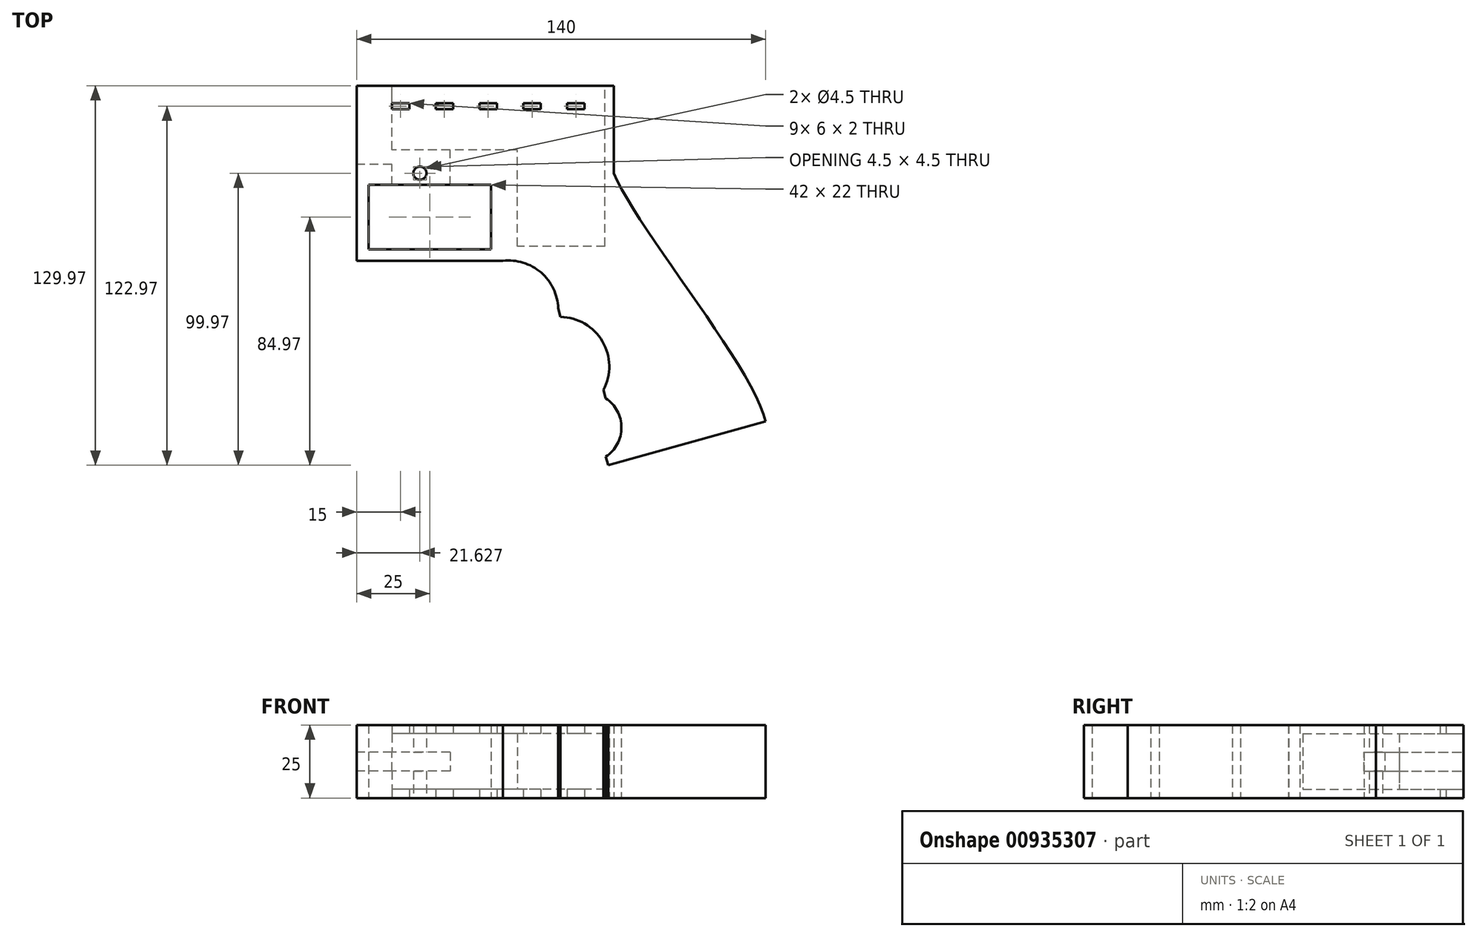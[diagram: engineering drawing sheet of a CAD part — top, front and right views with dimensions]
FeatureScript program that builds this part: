
annotation { "Feature Type Name" : "Feature", "Feature Type Description" : "" }
export const myFeature = defineFeature(function(context is Context, id is Id, definition is map)
    precondition{}
    {
        {
            var Q0;
            Q0=qCreatedBy(makeId("Top.planeOp"),FACE);
            var sketch = newSketch(context, id + "F0", { "sketchPlane" : qUnion([Q0])});
            skPoint(sketch, "E0", {"position": v(0, 0) * mm});
            skLineSegment(sketch, "E1.bottom", {"start": v(-44, 30) * mm, "end": v(44, 30) * mm});
            skLineSegment(sketch, "E1.top", {"start": v(-44, -30) * mm, "end": v(44, -30) * mm});
            skLineSegment(sketch, "E1.left", {"start": v(-44, 30) * mm, "end": v(-44, -30) * mm});
            skLineSegment(sketch, "E1.right", {"start": v(44, 30) * mm, "end": v(44, -30) * mm});
            skLineSegment(sketch, "E2.bottom", {"start": v(-40, -26) * mm, "end": v(2, -26) * mm});
            skLineSegment(sketch, "E2.top", {"start": v(-40, -4) * mm, "end": v(2, -4) * mm});
            skLineSegment(sketch, "E2.left", {"start": v(-40, -26) * mm, "end": v(-40, -4) * mm});
            skLineSegment(sketch, "E2.right", {"start": v(2, -26) * mm, "end": v(2, -4) * mm});
            skLineSegment(sketch, "E3.bottom", {"start": v(-32, 24) * mm, "end": v(-26, 24) * mm});
            skLineSegment(sketch, "E3.top", {"start": v(-32, 22) * mm, "end": v(-26, 22) * mm});
            skLineSegment(sketch, "E3.left", {"start": v(-32, 24) * mm, "end": v(-32, 22) * mm});
            skLineSegment(sketch, "E3.right", {"start": v(-26, 24) * mm, "end": v(-26, 22) * mm});
            skLineSegment(sketch, "E4.1.0.0", {"start": v(-17, 24) * mm, "end": v(-11, 24) * mm});
            skLineSegment(sketch, "E4.1.0.1", {"start": v(-17, 22) * mm, "end": v(-11, 22) * mm});
            skLineSegment(sketch, "E4.1.0.2", {"start": v(-11, 24) * mm, "end": v(-11, 22) * mm});
            skLineSegment(sketch, "E4.1.0.3", {"start": v(-17, 24) * mm, "end": v(-17, 22) * mm});
            skLineSegment(sketch, "E4.2.0.0", {"start": v(-2, 24) * mm, "end": v(4, 24) * mm});
            skLineSegment(sketch, "E4.2.0.1", {"start": v(-2, 22) * mm, "end": v(4, 22) * mm});
            skLineSegment(sketch, "E4.2.0.2", {"start": v(4, 24) * mm, "end": v(4, 22) * mm});
            skLineSegment(sketch, "E4.2.0.3", {"start": v(-2, 24) * mm, "end": v(-2, 22) * mm});
            skLineSegment(sketch, "E4.3.0.0", {"start": v(13, 24) * mm, "end": v(19, 24) * mm});
            skLineSegment(sketch, "E4.3.0.1", {"start": v(13, 22) * mm, "end": v(19, 22) * mm});
            skLineSegment(sketch, "E4.3.0.2", {"start": v(19, 24) * mm, "end": v(19, 22) * mm});
            skLineSegment(sketch, "E4.3.0.3", {"start": v(13, 24) * mm, "end": v(13, 22) * mm});
            skLineSegment(sketch, "E4.4.0.0", {"start": v(28, 24) * mm, "end": v(34, 24) * mm});
            skLineSegment(sketch, "E4.4.0.1", {"start": v(28, 22) * mm, "end": v(34, 22) * mm});
            skLineSegment(sketch, "E4.4.0.2", {"start": v(34, 24) * mm, "end": v(34, 22) * mm});
            skLineSegment(sketch, "E4.4.0.3", {"start": v(28, 24) * mm, "end": v(28, 22) * mm});
            skLineSegment(sketch, "E4.direction1", {"start": v(-32, 24) * mm, "end": v(-17, 24) * mm, "construction": true});
            skFitSpline(sketch, "E5", {"points": [v(44, 0) * mm, v(96, -85) * mm], "startDerivative": vector(23.47, -56.54) * mm, "endDerivative": vector(13.41, -56.5) * mm});
            skLineSegment(sketch, "E6", {"start": v(96, -85) * mm, "end": v(42.04, -99.97) * mm});
            skLineSegment(sketch, "E7", {"start": v(42.04, -99.97) * mm, "end": v(41.24, -97.08) * mm});
            skArc(sketch, "E8", {"start": v(41.24, -97.08) * mm, "mid": v(46.6, -87.08) * mm, "end": v(41.24, -77.08) * mm});
            skLineSegment(sketch, "E9", {"start": v(41.24, -77.08) * mm, "end": v(40.43, -74.2) * mm});
            skArc(sketch, "E10", {"start": v(40.43, -74.2) * mm, "mid": v(40.1, -57.58) * mm, "end": v(25.76, -49.2) * mm});
            skLineSegment(sketch, "E11", {"start": v(25.76, -49.2) * mm, "end": v(24.96, -46.3) * mm});
            skArc(sketch, "E12", {"start": v(24.96, -46.3) * mm, "mid": v(19.05, -34) * mm, "end": v(6, -30) * mm});
            skCircle(sketch, "E13", {"center": v(-22.37, 0) * mm, "radius": 2.25 * mm});
            skSolve(sketch);
        }
        {
            var Q0;
            {var subQ7=sQuery(id+"F0.wireOp",EDGE,"E1.bottom");Q0=makeQuery(id+"F0.imprint","IMPRINT",FACE,{"disambiguationData":[TD([[makeQuery(id+"F0.imprint","IMPRINT",EDGE,{"derivedFrom":subQ7}),-1.0]])]});}
            var Q1;
            {var subQ0=sQuery(id+"F0.wireOp",EDGE,"E5");Q1=makeQuery(id+"F0.imprint","IMPRINT",FACE,{"disambiguationData":[TD([[makeQuery(id+"F0.imprint","IMPRINT",EDGE,{"derivedFrom":subQ0}),-1.0]])]});}
            extrude(context, id + "F1", {"entities" : qUnion([Q0, Q1]), "depth" : 25 * mm, "offsetDistance" : 25 * mm});
        }
        {
            var Q0;
            Q0=makeQuery(id+"F1.opExtrude","SWEPT_FACE",FACE,{"disambiguationData":[OSD([sQuery(id+"F0.wireOp",EDGE,"E1.bottom")])]});
            var sketch = newSketch(context, id + "F2", { "sketchPlane" : qUnion([Q0])});
            skLineSegment(sketch, "E14.bottom", {"start": v(-41, 22) * mm, "end": v(32, 22) * mm});
            skLineSegment(sketch, "E14.top", {"start": v(-41, 3) * mm, "end": v(32, 3) * mm});
            skLineSegment(sketch, "E14.left", {"start": v(-41, 22) * mm, "end": v(-41, 3) * mm});
            skLineSegment(sketch, "E14.right", {"start": v(32, 22) * mm, "end": v(32, 3) * mm});
            skLineSegment(sketch, "E15", {"start": v(-11, 22) * mm, "end": v(-11, 3) * mm});
            skLineSegment(sketch, "E16.bottom", {"start": v(12, 15.75) * mm, "end": v(44, 15.75) * mm});
            skLineSegment(sketch, "E16.top", {"start": v(12, 9.25) * mm, "end": v(44, 9.25) * mm});
            skLineSegment(sketch, "E16.left", {"start": v(12, 15.75) * mm, "end": v(12, 9.25) * mm});
            skLineSegment(sketch, "E16.right", {"start": v(44, 15.75) * mm, "end": v(44, 9.25) * mm});
            skLineSegment(sketch, "E17", {"start": v(39.56, 15.75) * mm, "end": v(39.56, 25) * mm, "construction": true});
            skLineSegment(sketch, "E18", {"start": v(39.37, 9.25) * mm, "end": v(39.37, 0) * mm, "construction": true});
            skSolve(sketch);
        }
        {
            var Q0;
            {var subQ5=sQuery(id+"F2.wireOp",EDGE,"E16.right");Q0=makeQuery(id+"F2.imprint","IMPRINT",FACE,{"disambiguationData":[TD([[makeQuery(id+"F2.imprint","IMPRINT",EDGE,{"derivedFrom":subQ5}),-1.0]])]});}
            var Q1;
            {var subQ5=sQuery(id+"F2.wireOp",EDGE,"E16.left");Q1=makeQuery(id+"F2.imprint","IMPRINT",FACE,{"disambiguationData":[TD([[makeQuery(id+"F2.imprint","IMPRINT",EDGE,{"derivedFrom":subQ5}),1.0]])]});}
            var Q2;
            {var subQ9=sQuery(id+"F2.wireOp",EDGE,"E15");Q2=makeQuery(id+"F2.imprint","IMPRINT",FACE,{"disambiguationData":[TD([[makeQuery(id+"F2.imprint","IMPRINT",EDGE,{"derivedFrom":subQ9}),1.0]])]});}
            var Q3;
            {var subQ0=sQuery(id+"F2.wireOp",EDGE,"E14.left");Q3=makeQuery(id+"F2.imprint","IMPRINT",FACE,{"disambiguationData":[TD([[makeQuery(id+"F2.imprint","IMPRINT",EDGE,{"derivedFrom":subQ0}),1.0]])]});}
            extrude(context, id + "F3", {"entities" : qUnion([Q0, Q1, Q2, Q3]), "operationType" : NewBodyOperationType.REMOVE, "oppositeDirection" : true, "depth" : 22 * mm, "offsetDistance" : 25 * mm});
        }
        {
            var Q0;
            {var subQ0=sQuery(id+"F2.wireOp",EDGE,"E14.left");Q0=makeQuery(id+"F2.imprint","IMPRINT",FACE,{"disambiguationData":[TD([[makeQuery(id+"F2.imprint","IMPRINT",EDGE,{"derivedFrom":subQ0}),1.0]])]});}
            extrude(context, id + "F4", {"entities" : qUnion([Q0]), "operationType" : NewBodyOperationType.REMOVE, "oppositeDirection" : true, "depth" : 55 * mm, "offsetDistance" : 25 * mm});
        }
        {
            var Q0;
            {var subQ5=sQuery(id+"F2.wireOp",EDGE,"E16.left");Q0=makeQuery(id+"F2.imprint","IMPRINT",FACE,{"disambiguationData":[TD([[makeQuery(id+"F2.imprint","IMPRINT",EDGE,{"derivedFrom":subQ5}),1.0]])]});}
            var Q1;
            Q1=makeQuery(id+"F1.opExtrude","SWEPT_FACE",FACE,{"disambiguationData":[OSD([sQuery(id+"F0.wireOp",EDGE,"E2.top")])]});
            extrude(context, id + "F5", {"entities" : qUnion([Q0]), "operationType" : NewBodyOperationType.REMOVE, "endBound" : BoundingType.UP_TO_SURFACE, "oppositeDirection" : true, "depth" : 25 * mm, "endBoundEntityFace" : qUnion([Q1]), "offsetDistance" : 25 * mm});
        }
        {
            var Q0;
            {var subQ5=sQuery(id+"F2.wireOp",EDGE,"E16.right");Q0=makeQuery(id+"F2.imprint","IMPRINT",FACE,{"disambiguationData":[TD([[makeQuery(id+"F2.imprint","IMPRINT",EDGE,{"derivedFrom":subQ5}),-1.0]])]});}
            extrude(context, id + "F6", {"entities" : qUnion([Q0]), "operationType" : NewBodyOperationType.REMOVE, "oppositeDirection" : true, "depth" : 27 * mm, "offsetDistance" : 25 * mm});
        }
    });
